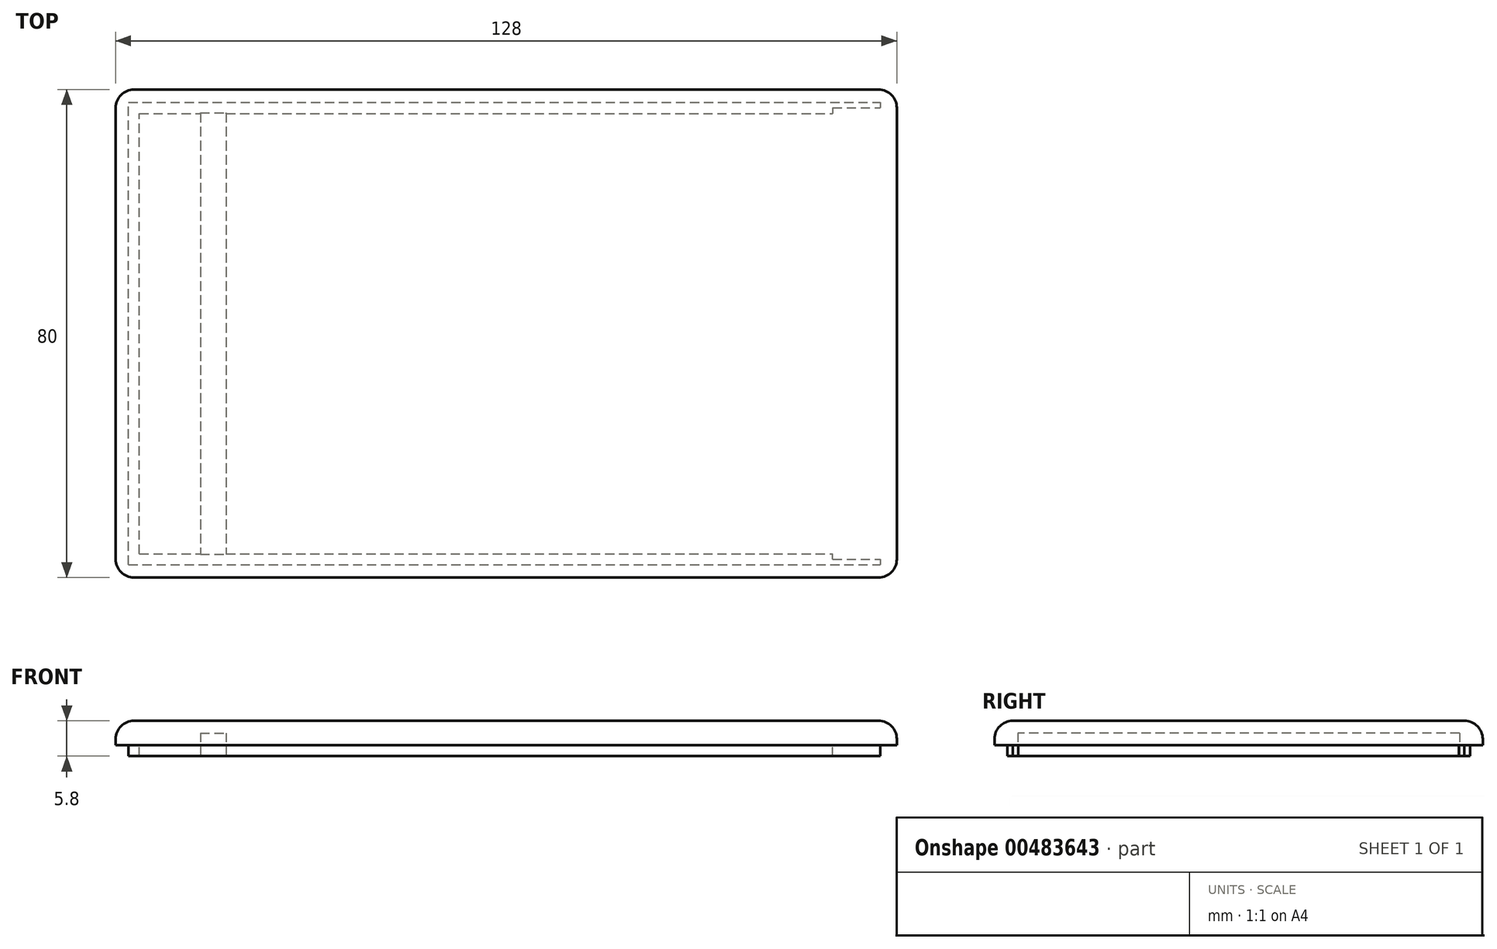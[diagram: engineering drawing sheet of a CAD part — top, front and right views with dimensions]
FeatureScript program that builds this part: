
annotation { "Feature Type Name" : "Feature", "Feature Type Description" : "" }
export const myFeature = defineFeature(function(context is Context, id is Id, definition is map)
    precondition{}
    {
        {
            var Q0;
            Q0=qCreatedBy(makeId("Top.planeOp"),FACE);
            var sketch = newSketch(context, id + "F0", { "sketchPlane" : qUnion([Q0])});
            skLineSegment(sketch, "E0.bottom", {"start": v(-64, 40) * mm, "end": v(64, 40) * mm});
            skLineSegment(sketch, "E0.top", {"start": v(-64, -40) * mm, "end": v(64, -40) * mm});
            skLineSegment(sketch, "E0.left", {"start": v(-64, 40) * mm, "end": v(-64, -40) * mm});
            skLineSegment(sketch, "E0.right", {"start": v(64, 40) * mm, "end": v(64, -40) * mm});
            skPoint(sketch, "E0.middle", {"position": v(0, 0) * mm});
            skSolve(sketch);
        }
        {
            var Q0;
            Q0 = qSketchRegion(id + "F0", true);
            extrude(context, id + "F1", {"entities" : qUnion([Q0]), "depth" : 4 * mm});
        }
        {
            var Q0;
            Q0=makeQuery(id+"F1.opExtrude","CAP_FACE",FACE,{"disambiguationData":[OSD([sQuery(id+"F0.wireOp",EDGE,"E0.bottom"),sQuery(id+"F0.wireOp",EDGE,"E0.top"),sQuery(id+"F0.wireOp",EDGE,"E0.left"),sQuery(id+"F0.wireOp",EDGE,"E0.right")])],"isStart":true});
            var sketch = newSketch(context, id + "F2", { "sketchPlane" : qUnion([Q0])});
            skPoint(sketch, "E1", {"position": v(-61.9, 37.9) * mm});
            skPoint(sketch, "E2", {"position": v(-61.9, -37.9) * mm});
            skLineSegment(sketch, "E3.bottom", {"start": v(-61.9, 37.9) * mm, "end": v(53.5, 37.9) * mm});
            skLineSegment(sketch, "E3.top", {"start": v(-61.9, 36.1) * mm, "end": v(53.5, 36.1) * mm});
            skLineSegment(sketch, "E3.left", {"start": v(-61.9, 37.9) * mm, "end": v(-61.9, 36.1) * mm});
            skLineSegment(sketch, "E3.right", {"start": v(53.5, 37.9) * mm, "end": v(53.5, 36.1) * mm});
            skLineSegment(sketch, "E4.bottom", {"start": v(-61.9, -37.9) * mm, "end": v(53.5, -37.9) * mm});
            skLineSegment(sketch, "E4.top", {"start": v(-61.9, -36.1) * mm, "end": v(53.5, -36.1) * mm});
            skLineSegment(sketch, "E4.left", {"start": v(-61.9, -37.9) * mm, "end": v(-61.9, -36.1) * mm});
            skLineSegment(sketch, "E4.right", {"start": v(53.5, -37.9) * mm, "end": v(53.5, -36.1) * mm});
            skPoint(sketch, "E5.oppositeSnap0", {"position": v(53.5, -37) * mm});
            skLineSegment(sketch, "E5.bottom", {"start": v(53.5, -37.9) * mm, "end": v(61.3, -37.9) * mm});
            skLineSegment(sketch, "E5.top", {"start": v(53.5, -37) * mm, "end": v(61.3, -37) * mm});
            skLineSegment(sketch, "E5.left", {"start": v(53.5, -37.9) * mm, "end": v(53.5, -37) * mm});
            skLineSegment(sketch, "E5.right", {"start": v(61.3, -37.9) * mm, "end": v(61.3, -37) * mm});
            skLineSegment(sketch, "E6.top", {"start": v(53.5, 37) * mm, "end": v(61.3, 37) * mm});
            skLineSegment(sketch, "E6.left", {"start": v(53.5, 36.1) * mm, "end": v(53.5, 37) * mm});
            skLineSegment(sketch, "E7.bottom", {"start": v(-61.9, 36.1) * mm, "end": v(-60.1, 36.1) * mm});
            skLineSegment(sketch, "E7.top", {"start": v(-61.9, -36.1) * mm, "end": v(-60.1, -36.1) * mm});
            skLineSegment(sketch, "E7.left", {"start": v(-61.9, 36.1) * mm, "end": v(-61.9, -36.1) * mm});
            skLineSegment(sketch, "E7.right", {"start": v(-60.1, 36.1) * mm, "end": v(-60.1, -36.1) * mm});
            skLineSegment(sketch, "E8", {"start": v(53.5, 37.9) * mm, "end": v(61.3, 37.9) * mm});
            skLineSegment(sketch, "E9", {"start": v(61.3, 37) * mm, "end": v(61.3, 37.9) * mm});
            skSolve(sketch);
        }
        {
            var Q0;
            Q0 = qSketchRegion(id + "F2", true);
            extrude(context, id + "F3", {"entities" : qUnion([Q0]), "operationType" : NewBodyOperationType.ADD, "depth" : 1.8 * mm});
        }
        {
            var Q0;
            Q0=makeQuery(id+"F1.opExtrude","CAP_FACE",FACE,{"disambiguationData":[OSD([sQuery(id+"F0.wireOp",EDGE,"E0.bottom"),sQuery(id+"F0.wireOp",EDGE,"E0.top"),sQuery(id+"F0.wireOp",EDGE,"E0.left"),sQuery(id+"F0.wireOp",EDGE,"E0.right")])],"isStart":true});
            var sketch = newSketch(context, id + "F4", { "sketchPlane" : qUnion([Q0])});
            skPoint(sketch, "E10", {"position": v(-50.1, -36.1) * mm});
            skPoint(sketch, "E11", {"position": v(-50.1, 36.1) * mm});
            skPoint(sketch, "E12", {"position": v(-45.9, 36.1) * mm});
            skPoint(sketch, "E13", {"position": v(-45.9, -36.1) * mm});
            skLineSegment(sketch, "E14.bottom", {"start": v(-50.1, -36.1) * mm, "end": v(-45.9, -36.1) * mm});
            skLineSegment(sketch, "E14.top", {"start": v(-50.1, 36.1) * mm, "end": v(-45.9, 36.1) * mm});
            skLineSegment(sketch, "E14.left", {"start": v(-50.1, -36.1) * mm, "end": v(-50.1, 36.1) * mm});
            skLineSegment(sketch, "E14.right", {"start": v(-45.9, -36.1) * mm, "end": v(-45.9, 36.1) * mm});
            skSolve(sketch);
        }
        {
            var Q0;
            Q0 = qSketchRegion(id + "F4", true);
            extrude(context, id + "F5", {"entities" : qUnion([Q0]), "operationType" : NewBodyOperationType.REMOVE, "oppositeDirection" : true, "depth" : 2 * mm});
        }
        {
            var Q0;
            Q0=makeQuery(id+"F3.opExtrude","CAP_FACE",FACE,{"disambiguationData":[OSD([sQuery(id+"F2.wireOp",EDGE,"E3.bottom"),sQuery(id+"F2.wireOp",EDGE,"E3.top"),sQuery(id+"F2.wireOp",EDGE,"E3.left"),sQuery(id+"F2.wireOp",EDGE,"E3.right"),sQuery(id+"F2.wireOp",EDGE,"E4.bottom"),sQuery(id+"F2.wireOp",EDGE,"E4.top"),sQuery(id+"F2.wireOp",EDGE,"E4.left"),sQuery(id+"F2.wireOp",EDGE,"E4.right"),sQuery(id+"F2.wireOp",EDGE,"E5.bottom"),sQuery(id+"F2.wireOp",EDGE,"E5.top"),sQuery(id+"F2.wireOp",EDGE,"E5.right"),sQuery(id+"F2.wireOp",EDGE,"E6.bottom"),sQuery(id+"F2.wireOp",EDGE,"E6.top"),sQuery(id+"F2.wireOp",EDGE,"E6.right"),sQuery(id+"F2.wireOp",EDGE,"E7.left"),sQuery(id+"F2.wireOp",EDGE,"E7.right")])],"isStart":false});
            var sketch = newSketch(context, id + "F6", { "sketchPlane" : qUnion([Q0])});
            skPoint(sketch, "E15", {"position": v(-50.1, -36.1) * mm});
            skPoint(sketch, "E16", {"position": v(-60.1, -36.1) * mm});
            skPoint(sketch, "E17", {"position": v(-61.9, 36.1) * mm});
            skPoint(sketch, "E18", {"position": v(-50.1, 36.1) * mm});
            skLineSegment(sketch, "E19.bottom", {"start": v(-50.1, 36.1) * mm, "end": v(-45.9, 36.1) * mm});
            skLineSegment(sketch, "E19.top", {"start": v(-50.1, 36.2) * mm, "end": v(-45.9, 36.2) * mm});
            skLineSegment(sketch, "E19.left", {"start": v(-50.1, 36.1) * mm, "end": v(-50.1, 36.2) * mm});
            skLineSegment(sketch, "E19.right", {"start": v(-45.9, 36.1) * mm, "end": v(-45.9, 36.2) * mm});
            skPoint(sketch, "E20", {"position": v(-60.1, 36.1) * mm});
            skPoint(sketch, "E21", {"position": v(-61.9, -34.12) * mm});
            skLineSegment(sketch, "E22.bottom", {"start": v(-50.1, -36.1) * mm, "end": v(-45.9, -36.1) * mm});
            skLineSegment(sketch, "E22.top", {"start": v(-50.1, -36.2) * mm, "end": v(-45.9, -36.2) * mm});
            skLineSegment(sketch, "E22.left", {"start": v(-50.1, -36.1) * mm, "end": v(-50.1, -36.2) * mm});
            skLineSegment(sketch, "E22.right", {"start": v(-45.9, -36.1) * mm, "end": v(-45.9, -36.2) * mm});
            skSolve(sketch);
        }
        {
            var Q0;
            Q0 = qSketchRegion(id + "F6", true);
            extrude(context, id + "F7", {"entities" : qUnion([Q0]), "operationType" : NewBodyOperationType.REMOVE, "oppositeDirection" : true, "depth" : 3.8 * mm});
        }
        {
            var Q0;
            Q0=makeQuery(id+"F1.opExtrude","SWEPT_EDGE",EDGE,{"disambiguationData":[OSD([sQuery(id+"F0.wireOp",EDGE,"E0.top"),sQuery(id+"F0.wireOp",EDGE,"E0.right")])]});
            var Q1;
            Q1=makeQuery(id+"F1.opExtrude","SWEPT_EDGE",EDGE,{"disambiguationData":[OSD([sQuery(id+"F0.wireOp",EDGE,"E0.bottom"),sQuery(id+"F0.wireOp",EDGE,"E0.right")])]});
            var Q2;
            Q2=makeQuery(id+"F1.opExtrude","SWEPT_EDGE",EDGE,{"disambiguationData":[OSD([sQuery(id+"F0.wireOp",EDGE,"E0.bottom"),sQuery(id+"F0.wireOp",EDGE,"E0.left")])]});
            var Q3;
            Q3=makeQuery(id+"F1.opExtrude","SWEPT_EDGE",EDGE,{"disambiguationData":[OSD([sQuery(id+"F0.wireOp",EDGE,"E0.top"),sQuery(id+"F0.wireOp",EDGE,"E0.left")])]});
            var Q4;
            Q4=makeQuery(id+"F1.opExtrude","CAP_EDGE",EDGE,{"disambiguationData":[OSD([sQuery(id+"F0.wireOp",EDGE,"E0.top")])],"isStart":false});
            var Q5;
            Q5=makeQuery(id+"F1.opExtrude","CAP_EDGE",EDGE,{"disambiguationData":[OSD([sQuery(id+"F0.wireOp",EDGE,"E0.left")])],"isStart":false});
            var Q6;
            Q6=makeQuery(id+"F1.opExtrude","CAP_EDGE",EDGE,{"disambiguationData":[OSD([sQuery(id+"F0.wireOp",EDGE,"E0.bottom")])],"isStart":false});
            var Q7;
            Q7=makeQuery(id+"F1.opExtrude","CAP_EDGE",EDGE,{"disambiguationData":[OSD([sQuery(id+"F0.wireOp",EDGE,"E0.right")])],"isStart":false});
            fillet(context, id + "F8", {"entities" : qUnion([Q0, Q1, Q2, Q3, Q4, Q5, Q6, Q7]), "radius" : 3 * mm, "tangentPropagation" : true, "allowEdgeOverflow" : false});
        }
    });
